# Revit family: PX_SEQ-EXT-Surface-4All-Channel_And_Galv-Steel-Grate-1m_PC033098
name_source: partatom
category: Plumbing Fixtures
revit_build: Autodesk Revit 2016 (Build: 20190507_1515(x64)
units: mm (PartAtom-declared; Revit-internal decimal feet)

## family parameters
Always vertical = Yes
Cut with Voids When Loaded = No
Part Type = Normal
Room Calculation Point = No
Round Connector Dimension = Use Diameter
Shared = No
Work Plane-Based = No

## types (1)
- SEAQUAL 4All Channel & Galv Steel Grate 1m PC 033098
    Made By = Tolani Civil Projects cc
    Manufacturer = Seaqual
    Model = 033098
    Note = 4All Channel & Grate 1m is perfect for selection in areas where a 3m Garage Pack would not be sufficient such as patios & "stoeps", around swimming pools & along garden / pedestrian pathways longer than three running meters. The loose Channels & Grates also carry vehicular weight up to 1.5T.

Grate options include Black HD-PE and Galvanised Steel.
    PVC Black = PVC Black
    SS = SS
    Tolani Civil Projects cc URL = http://www.tcpbim.co.za
    Type Comments = 4All Channel & Galv Steel Grate 1m
    URL = https://seaqual.co.za

## geometry (parser evidence)
native form markers: Sweep x2
no freeform markers — native parametric forms only
